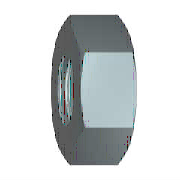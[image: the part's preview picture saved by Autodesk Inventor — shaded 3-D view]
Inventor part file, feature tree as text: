
AUTODESK INVENTOR PART (.ipt)
format: ipt  version: 2023 (Build 270158000, 158)  size: 162,816 bytes
history: native  units: mm (DEFAULTED — no unit token found)
features: sketch x3, other x2, extrude x1, hole x1, plane x1
ambient origin geometry x7: Origin, YZ Plane, XZ Plane, X Axis, Y Axis, Z Axis, Center Point
bodies: Solid1 (feature_tree)
feature tree (8):
  extrude  "Базовый элемент"  Depth=11.547005mm
  other  "Фаска1"
  hole  "Резьба"  [1 undecoded]
  other  "Work Axis1"
  plane  "Work Plane1"
  sketch  "Эскиз1"
  sketch  "Эскиз2"
  sketch  "Эскиз3"
note: 1 required parameter value undecoded (feature->parameter linkage not recoverable at this tier; creation-order binding heuristic only, values carry confidence <= 0.55)
